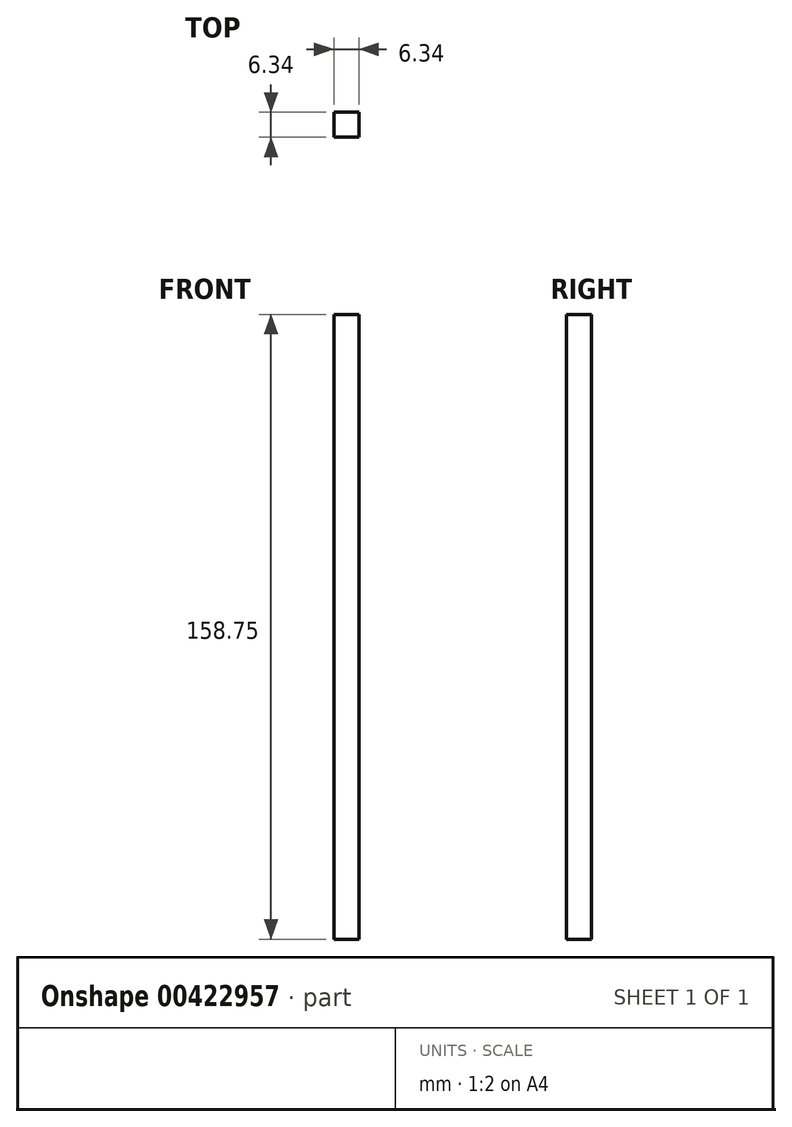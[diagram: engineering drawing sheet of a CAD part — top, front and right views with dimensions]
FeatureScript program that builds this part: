
annotation { "Feature Type Name" : "Feature", "Feature Type Description" : "" }
export const myFeature = defineFeature(function(context is Context, id is Id, definition is map)
    precondition{}
    {
        {
            var Q0;
            Q0=qCreatedBy(makeId("Top.planeOp"),FACE);
            var sketch = newSketch(context, id + "F0", { "sketchPlane" : qUnion([Q0])});
            skLineSegment(sketch, "E0.bottom", {"start": v(3.18, 3.17) * mm, "end": v(-3.17, 3.17) * mm});
            skLineSegment(sketch, "E0.top", {"start": v(3.18, -3.18) * mm, "end": v(-3.18, -3.18) * mm});
            skLineSegment(sketch, "E0.left", {"start": v(3.18, 3.17) * mm, "end": v(3.18, -3.18) * mm});
            skLineSegment(sketch, "E0.right", {"start": v(-3.18, 3.17) * mm, "end": v(-3.18, -3.17) * mm});
            skPoint(sketch, "E0.middle", {"position": v(0, 0) * mm});
            skSolve(sketch);
        }
        {
            var Q0;
            Q0 = qSketchRegion(id + "F0", true);
            extrude(context, id + "F1", {"entities" : qUnion([Q0]), "depth" : 158.75 * mm, "offsetDistance" : 25.4 * mm});
        }
    });
